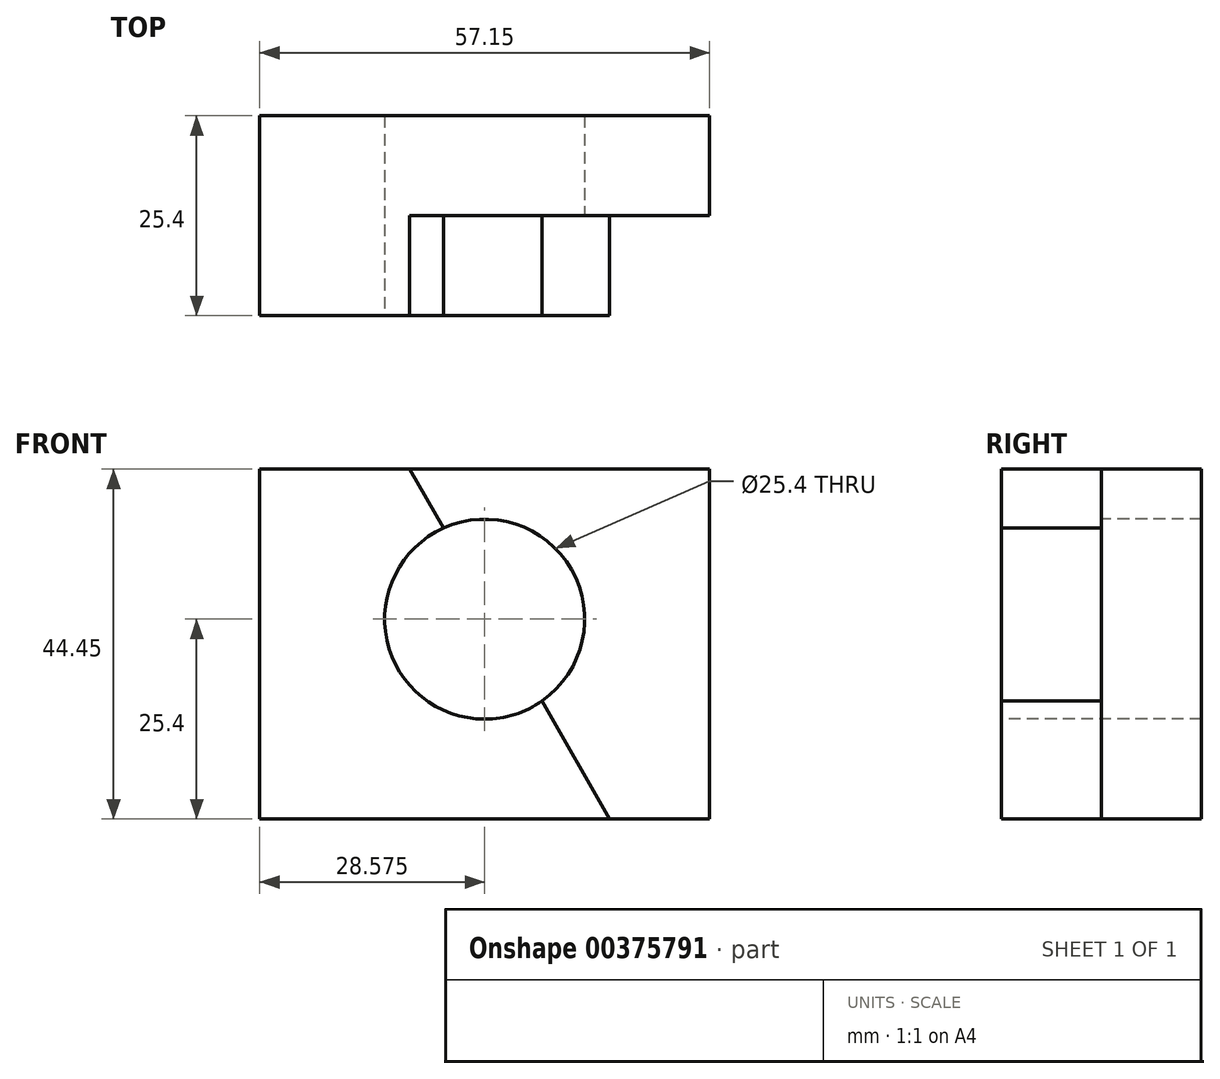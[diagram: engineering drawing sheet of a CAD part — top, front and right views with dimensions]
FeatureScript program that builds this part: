
annotation { "Feature Type Name" : "Feature", "Feature Type Description" : "" }
export const myFeature = defineFeature(function(context is Context, id is Id, definition is map)
    precondition{}
    {
        {
            var Q0;
            Q0=qCreatedBy(makeId("Right.planeOp"),FACE);
            var sketch = newSketch(context, id + "F0", { "sketchPlane" : qUnion([Q0])});
            skLineSegment(sketch, "E0", {"start": v(0, 0) * mm, "end": v(25.4, 0) * mm});
            skLineSegment(sketch, "E1", {"start": v(25.4, 0) * mm, "end": v(25.4, 44.45) * mm});
            skLineSegment(sketch, "E2", {"start": v(25.4, 44.45) * mm, "end": v(0, 44.45) * mm});
            skLineSegment(sketch, "E3", {"start": v(0, 44.45) * mm, "end": v(0, 0) * mm});
            skSolve(sketch);
        }
        {
            var Q0;
            Q0=makeQuery(id+"F0.imprint","IMPRINT",FACE,{"disambiguationData":[TD([[makeQuery(id+"F0.imprint","IMPRINT",EDGE,{"derivedFrom":sQuery(id+"F0.wireOp",EDGE,"E0")}),1.0]])]});
            extrude(context, id + "F1", {"entities" : qUnion([Q0]), "depth" : 57.15 * mm});
        }
        {
            var Q0;
            Q0=makeQuery(id+"F1.opExtrude","SWEPT_FACE",FACE,{"disambiguationData":[OSD([sQuery(id+"F0.wireOp",EDGE,"E3")])]});
            var sketch = newSketch(context, id + "F2", { "sketchPlane" : qUnion([Q0])});
            skCircle(sketch, "E4", {"center": v(28.58, 25.4) * mm, "radius": 12.7 * mm});
            skPoint(sketch, "E4.centerSnap0", {"position": v(28.58, 44.45) * mm});
            skSolve(sketch);
        }
        {
            var Q0;
            Q0=makeQuery(id+"F2.imprint","IMPRINT",FACE,{"disambiguationData":[TD([[makeQuery(id+"F2.imprint","IMPRINT",EDGE,{"derivedFrom":sQuery(id+"F2.wireOp",EDGE,"E4")}),1.0]])]});
            extrude(context, id + "F3", {"entities" : qUnion([Q0]), "operationType" : NewBodyOperationType.REMOVE, "oppositeDirection" : true, "depth" : 25.4 * mm});
        }
        {
            var Q0;
            Q0=makeQuery(id+"F1.opExtrude","SWEPT_FACE",FACE,{"disambiguationData":[OSD([sQuery(id+"F0.wireOp",EDGE,"E3")])]});
            var sketch = newSketch(context, id + "F4", { "sketchPlane" : qUnion([Q0])});
            skLineSegment(sketch, "E5", {"start": v(44.45, 44.45) * mm, "end": v(44.45, 0) * mm});
            skLineSegment(sketch, "E6", {"start": v(44.45, 0) * mm, "end": v(19.05, 44.45) * mm});
            skSolve(sketch);
        }
        {
            var Q0;
            {var subQ6=sQuery(id+"F4.wireOp",EDGE,"E5");Q0=makeQuery(id+"F4.imprint","IMPRINT",FACE,{"disambiguationData":[TD([[makeQuery(id+"F4.imprint","IMPRINT",EDGE,{"derivedFrom":subQ6}),-1.0]])]});}
            var Q1;
            {var subQ0=sQuery(id+"F4.wireOp",EDGE,"E5");Q1=makeQuery(id+"F4.imprint","IMPRINT",FACE,{"disambiguationData":[TD([[makeQuery(id+"F4.imprint","IMPRINT",EDGE,{"derivedFrom":subQ0}),1.0]])]});}
            extrude(context, id + "F5", {"entities" : qUnion([Q0, Q1]), "operationType" : NewBodyOperationType.REMOVE, "oppositeDirection" : true, "depth" : 12.7 * mm});
        }
    });
